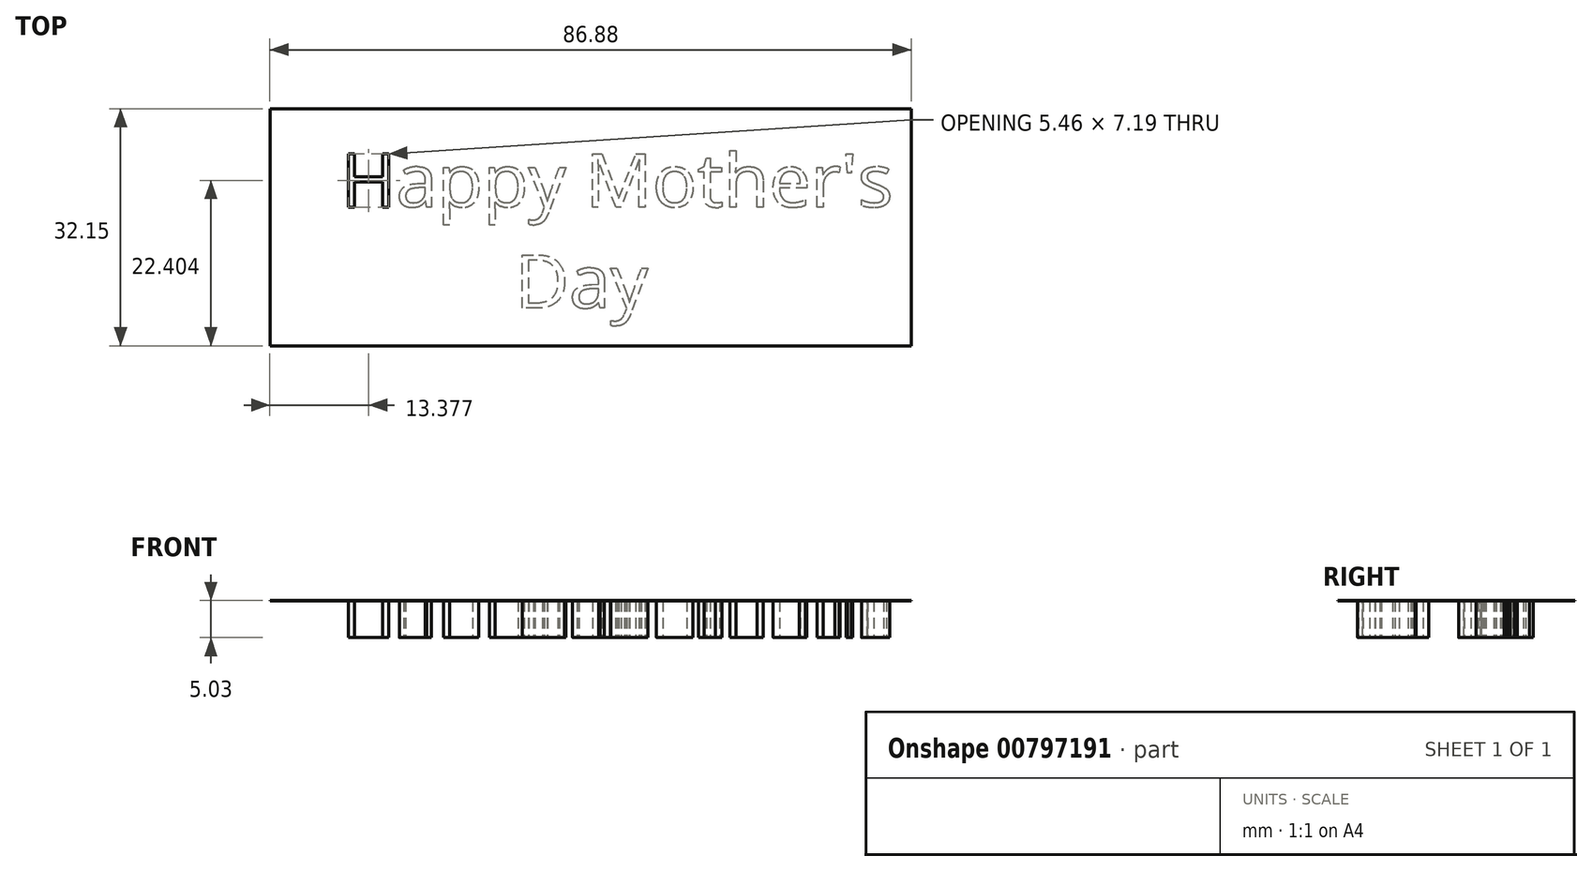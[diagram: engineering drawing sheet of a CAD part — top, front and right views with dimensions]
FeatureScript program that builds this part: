
annotation { "Feature Type Name" : "Feature", "Feature Type Description" : "" }
export const myFeature = defineFeature(function(context is Context, id is Id, definition is map)
    precondition{}
    {
        {
            var Q0;
            Q0=qCreatedBy(makeId("Top.planeOp"),FACE);
            var sketch = newSketch(context, id + "F0", { "sketchPlane" : qUnion([Q0])});
            skText(sketch, "E0", { "text": "Happy Mother\'s\n         Day", "fontName": "OpenSans-Regular.ttf"});
            const initialGuessF0  = {"E0": [-0.00516, -0.00346, 1, 0, 0.00725]};
            skSetInitialGuess(sketch, initialGuessF0);
            skSolve(sketch);
        }
        {
            var Q0;
            Q0 = qSketchRegion(id + "F0", true);
            extrude(context, id + "F1", {"entities" : qUnion([Q0]), "depth" : 5 * mm, "offsetDistance" : 25.4 * mm});
        }
        {
            var Q0;
            Q0=makeQuery(id+"F1.opExtrude","CAP_FACE",FACE,{"disambiguationData":[OSD([sQuery(id+"F0.wireOp",EDGE,"E0.sketch_text.stroke-0"),sQuery(id+"F0.wireOp",EDGE,"E0.sketch_text.stroke-1"),sQuery(id+"F0.wireOp",EDGE,"E0.sketch_text.stroke-2"),sQuery(id+"F0.wireOp",EDGE,"E0.sketch_text.stroke-3"),sQuery(id+"F0.wireOp",EDGE,"E0.sketch_text.stroke-4"),sQuery(id+"F0.wireOp",EDGE,"E0.sketch_text.stroke-5"),sQuery(id+"F0.wireOp",EDGE,"E0.sketch_text.stroke-6"),sQuery(id+"F0.wireOp",EDGE,"E0.sketch_text.stroke-7"),sQuery(id+"F0.wireOp",EDGE,"E0.sketch_text.stroke-8"),sQuery(id+"F0.wireOp",EDGE,"E0.sketch_text.stroke-9"),sQuery(id+"F0.wireOp",EDGE,"E0.sketch_text.stroke-10"),sQuery(id+"F0.wireOp",EDGE,"E0.sketch_text.stroke-11")])],"isStart":false});
            var sketch = newSketch(context, id + "F2", { "sketchPlane" : qUnion([Q0])});
            skLineSegment(sketch, "E1.bottom", {"start": v(-14.82, 9.88) * mm, "end": v(72.06, 9.88) * mm});
            skLineSegment(sketch, "E1.top", {"start": v(-14.82, -22.27) * mm, "end": v(72.06, -22.27) * mm});
            skLineSegment(sketch, "E1.left", {"start": v(-14.82, 9.88) * mm, "end": v(-14.82, -22.27) * mm});
            skLineSegment(sketch, "E1.right", {"start": v(72.06, 9.88) * mm, "end": v(72.06, -22.27) * mm});
            skSolve(sketch);
        }
        {
            var Q0;
            Q0=makeQuery(id+"F2.imprint","IMPRINT",FACE,{"disambiguationData":[TD([[makeQuery(id+"F2.imprint","IMPRINT",EDGE,{"derivedFrom":sQuery(id+"F2.wireOp",EDGE,"E1.bottom")}),-1.0]])]});
            extrude(context, id + "F3", {"entities" : qUnion([Q0]), "operationType" : NewBodyOperationType.ADD, "depth" : 0.03 * mm, "offsetDistance" : 25.4 * mm});
        }
    });
